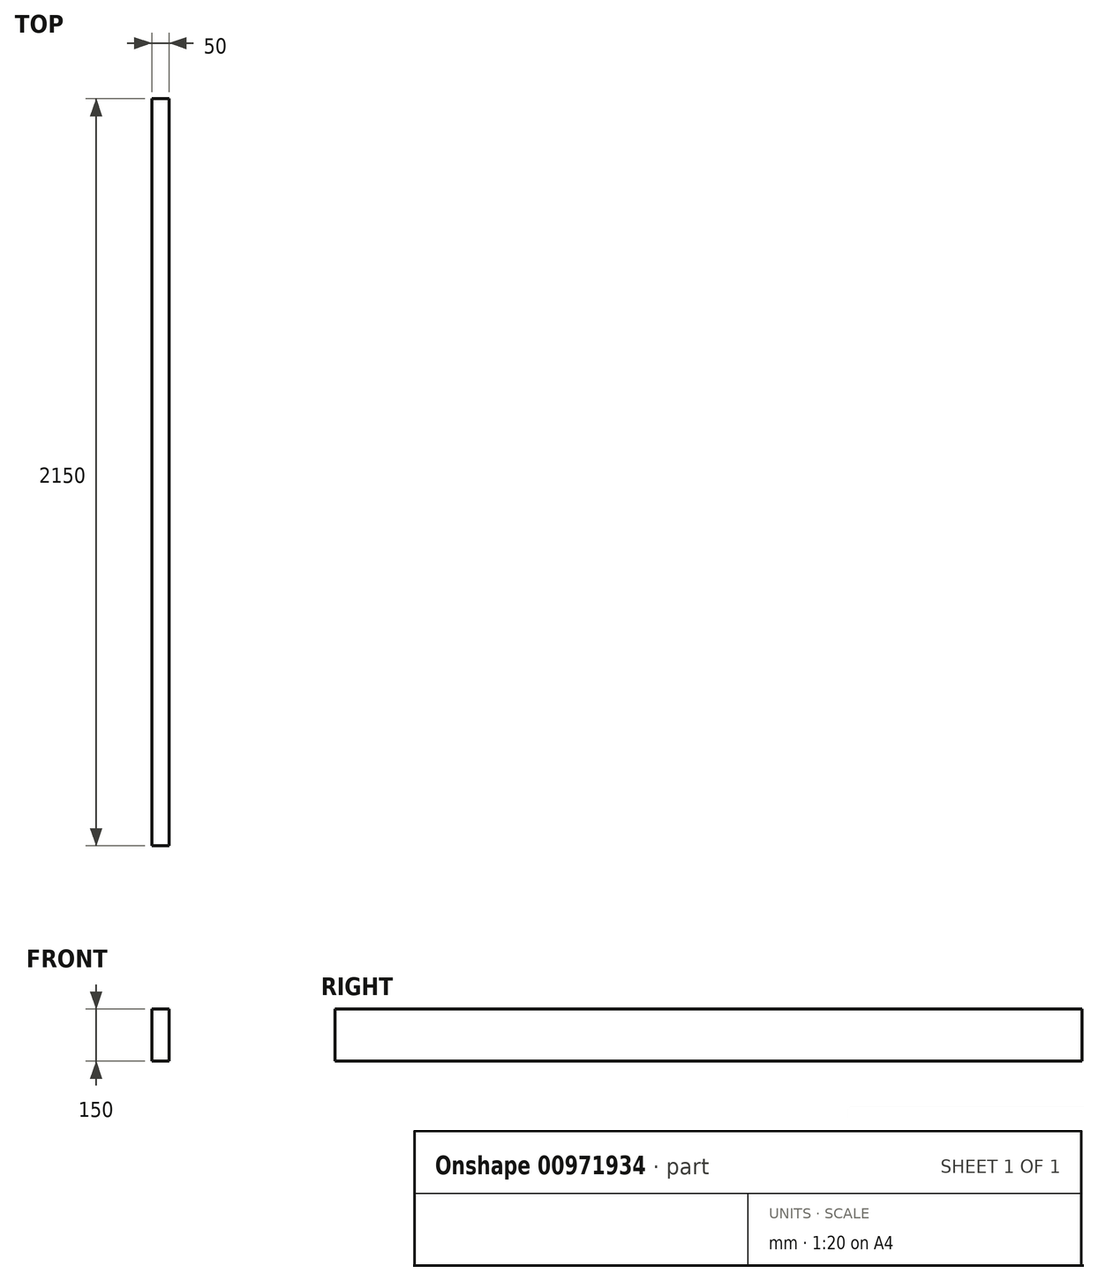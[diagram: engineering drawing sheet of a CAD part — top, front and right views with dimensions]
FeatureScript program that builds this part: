
annotation { "Feature Type Name" : "Feature", "Feature Type Description" : "" }
export const myFeature = defineFeature(function(context is Context, id is Id, definition is map)
    precondition{}
    {
        {
            var Q0;
            Q0=qCreatedBy(makeId("Front.planeOp"),FACE);
            var sketch = newSketch(context, id + "F0", { "sketchPlane" : qUnion([Q0])});
            skLineSegment(sketch, "E0.bottom", {"start": v(25, -75) * mm, "end": v(-25, -75) * mm});
            skLineSegment(sketch, "E0.top", {"start": v(25, 75) * mm, "end": v(-25, 75) * mm});
            skLineSegment(sketch, "E0.left", {"start": v(25, -75) * mm, "end": v(25, 75) * mm});
            skLineSegment(sketch, "E0.right", {"start": v(-25, -75) * mm, "end": v(-25, 75) * mm});
            skPoint(sketch, "E0.middle", {"position": v(0, 0) * mm});
            skSolve(sketch);
        }
        {
            var Q0;
            Q0 = qSketchRegion(id + "F0", true);
            extrude(context, id + "F1", {"entities" : qUnion([Q0]), "depth" : 2150 * mm, "offsetDistance" : 25 * mm});
        }
    });
